# Revit family: Seating-LAMMHULTS-GRADE_PLUS-Wooden_frame
name_source: partatom
category: Furniture
revit_build: Autodesk Revit 2017 (Build: 20170816_0615(x64)
units: mm (PartAtom-declared; Revit-internal decimal feet)

## family parameters
Always vertical = Yes
Cut with Voids When Loaded = No
OmniClass Number = 23.40.20.00
OmniClass Title = General Furniture and Specialties
Room Calculation Point = No
Shared = No
Work Plane-Based = No

## types (3) — shared parameters
Assembly Code = E2020
Depth = 550 mm
Description = *Please enter mtrl description here for use in mto*
Height = 800 mm  [stored 2.62467 ft]
Keynote = 46.B
Legs Material = Wood - Veneer - Birch
Manufacturer = LAMMHULTS
Model = *Furniture model*
URL = www.lammhults.se
Weight = 5.2 kg
Width = 590 mm  [stored 1.9357 ft]

## per-type parameters (varying)
| type | Seat Material | Seat Pad Material |
| White | Plastic - White | Colour - Khaki |
| Black | Plastic - Black | Colour - Khaki |
| Red | Plastic - Red | Fabric - Red |

note: [stored X ft] marks values corroborated as IEEE doubles in the binary element streams (Revit-internal decimal feet)

## geometry (parser evidence)
native form markers: Blend x14, Sweep x2
no freeform markers — native parametric forms only
